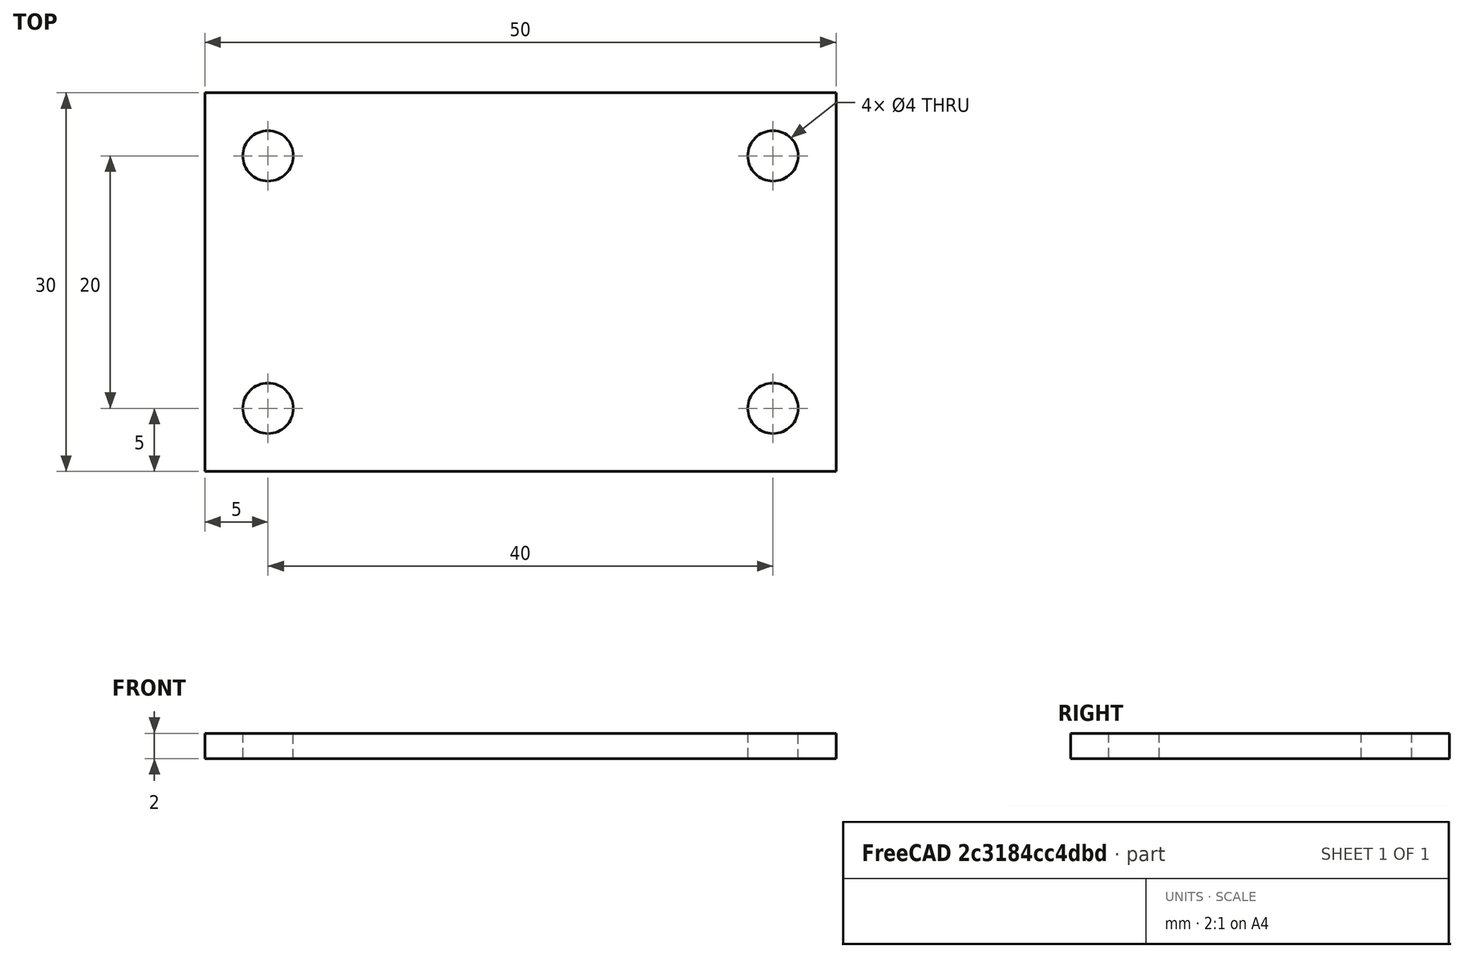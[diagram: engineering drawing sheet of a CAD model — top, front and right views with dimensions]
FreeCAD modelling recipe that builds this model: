
FCSTD DOCUMENT  (FreeCAD 1.1R20251125 (Git shallow))
Label: lesson7
License: All rights reserved
LicenseURL: https://en.wikipedia.org/wiki/All_rights_reserved
objects: App::Point×1, Sketcher::SketchObject×1, PartDesign::Pad×1, PartDesign::Body×1
note: 6 computed .brp shape members not serialized (recipe doc carries the construction recipe); baked Part::Feature solids carry a one-line shape summary decoded from their .brp

FEATURE [App::Point] Origin001
  Role = Origin
FEATURE [Sketcher::SketchObject] Sketch
  ArcFitTolerance = 1e-06
  AttachmentSupport = -> [Origin]
  ExternalTypes = [0]
  FullyConstrained = true
  MakeInternals = false
  MapMode = 5
  sketch-geometry (8):
    g0: LineSegment StartX=-25 StartY=15 StartZ=0 EndX=-25 EndY=-15 EndZ=0
    g1: LineSegment StartX=-25 StartY=-15 StartZ=0 EndX=25 EndY=-15 EndZ=0
    g2: LineSegment StartX=25 StartY=-15 StartZ=0 EndX=25 EndY=15 EndZ=0
    g3: LineSegment StartX=25 StartY=15 StartZ=0 EndX=-25 EndY=15 EndZ=0
    g4: Circle CenterX=-20 CenterY=10 CenterZ=0 NormalX=0 NormalY=0 NormalZ=1 AngleXU=0 Radius=2
    g5: Circle CenterX=20 CenterY=10 CenterZ=0 NormalX=0 NormalY=0 NormalZ=1 AngleXU=0 Radius=2
    g6: Circle CenterX=20 CenterY=-10 CenterZ=0 NormalX=0 NormalY=0 NormalZ=1 AngleXU=0 Radius=2
    g7: Circle CenterX=-20 CenterY=-10 CenterZ=0 NormalX=0 NormalY=0 NormalZ=1 AngleXU=0 Radius=2
  constraints (23):
    c: Coincident(g0,g1)
    c: Coincident(g1,g2)
    c: Coincident(g2,g3)
    c: Coincident(g3,g0)
    c: Vertical(g0)
    c: Vertical(g2)
    c: Horizontal(g1)
    c: Horizontal(g3)
    c: DistanceX(g3,g3) = 50
    c: DistanceY(g0,g0) = 30
    c: Symmetric(g0,g1,g-1)
    c: Equal(g4,g7)
    c: Equal(g7,g6)
    c: Equal(g6,g5)
    c: Distance(g4,g0) = 5
    c: DistanceY(g4,g0) = 5
    c: Diameter(g4) = 4
    c: DistanceY(g1,g6) = 5
    c: DistanceX(g6,g1) = 5
    c: Vertical(g4,g7)
    c: Horizontal(g4,g5)
    c: Horizontal(g6,g7)
    c: Vertical(g5,g6)
FEATURE [PartDesign::Pad] Pad
  Direction = (0,0,1)
  Length = 2
  Length2 = 10
  Profile = -> Sketch
  ReferenceAxis = -> Sketch [N_Axis]
  Refine = true
  SideType = 0
  Suppressed = false
  Type = 0
  Type2 = 0
FEATURE [PartDesign::Body] Body
  AllowCompound = true
  Group = -> [Sketch,Pad]
  Origin = -> Origin
  Tip = -> Pad
